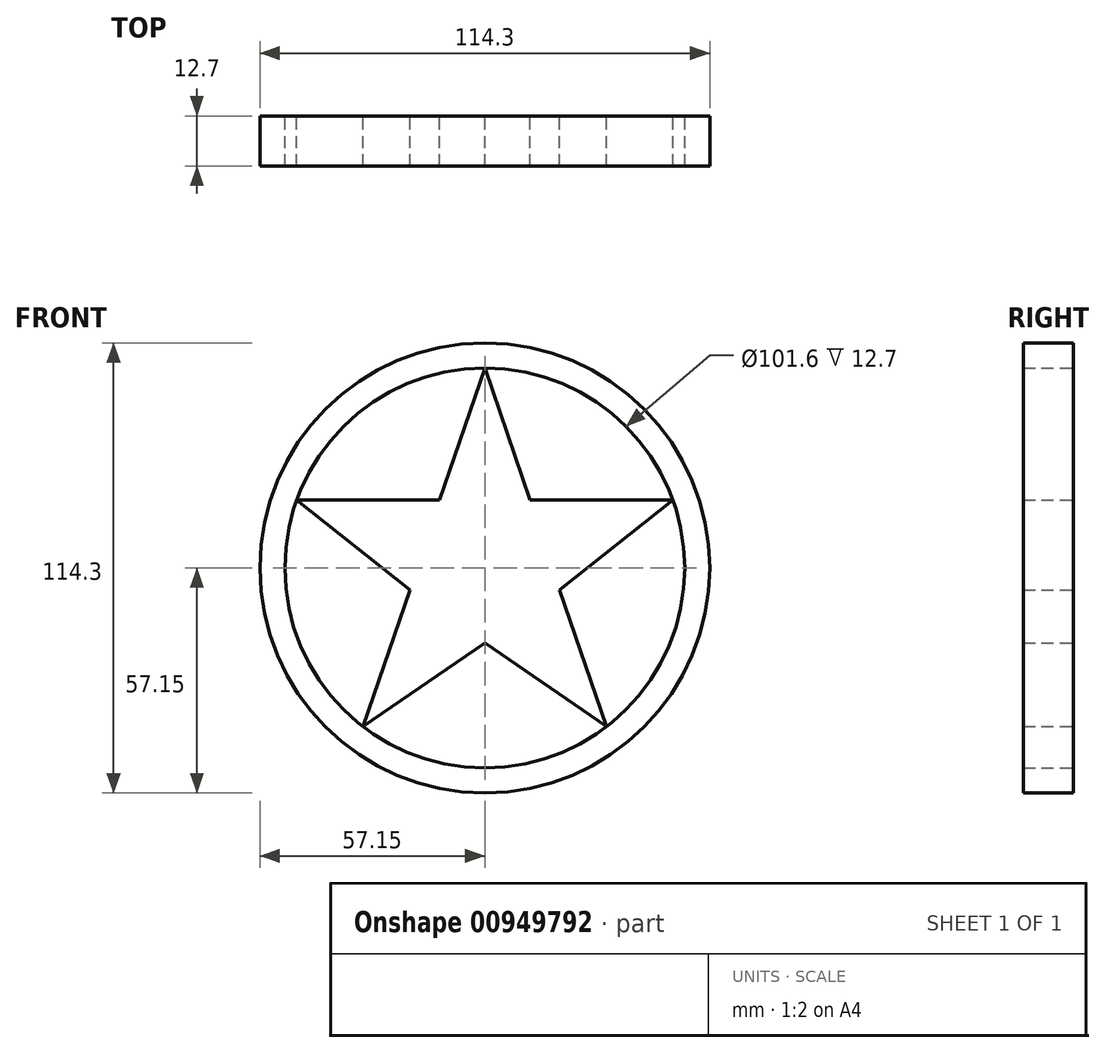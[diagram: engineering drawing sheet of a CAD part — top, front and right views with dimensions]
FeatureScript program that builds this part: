
annotation { "Feature Type Name" : "Feature", "Feature Type Description" : "" }
export const myFeature = defineFeature(function(context is Context, id is Id, definition is map)
    precondition{}
    {
        {
            var Q0;
            Q0=qCreatedBy(makeId("Front.planeOp"),FACE);
            var sketch = newSketch(context, id + "F0", { "sketchPlane" : qUnion([Q0])});
            skCircle(sketch, "E0", {"center": v(0, 0) * mm, "radius": 50.8 * mm});
            skLineSegment(sketch, "E1", {"start": v(0, 50.8) * mm, "end": v(-11.5, 17.3) * mm});
            skLineSegment(sketch, "E2", {"start": v(-11.5, 17.3) * mm, "end": v(-47.76, 17.3) * mm});
            skLineSegment(sketch, "E3", {"start": v(-47.76, 17.3) * mm, "end": v(-19, -5.57) * mm});
            skLineSegment(sketch, "E4", {"start": v(-19, -5.57) * mm, "end": v(-30.93, -40.3) * mm});
            skLineSegment(sketch, "E5", {"start": v(-30.93, -40.3) * mm, "end": v(0, -19.07) * mm});
            skLineSegment(sketch, "E6", {"start": v(0, 91.53) * mm, "end": v(0, -94.74) * mm, "construction": true});
            skLineSegment(sketch, "E7.MirrorCS", {"start": v(30.93, -40.3) * mm, "end": v(0, -19.07) * mm});
            skLineSegment(sketch, "E8.MirrorCS", {"start": v(19, -5.57) * mm, "end": v(30.93, -40.3) * mm});
            skLineSegment(sketch, "E9.MirrorCS", {"start": v(47.76, 17.3) * mm, "end": v(19, -5.57) * mm});
            skLineSegment(sketch, "E10.MirrorCS", {"start": v(0, 50.8) * mm, "end": v(11.5, 17.3) * mm});
            skLineSegment(sketch, "E11.MirrorCS", {"start": v(11.5, 17.3) * mm, "end": v(47.76, 17.3) * mm});
            skCircle(sketch, "E12", {"center": v(0, 0) * mm, "radius": 57.15 * mm});
            skSolve(sketch);
        }
        {
            var Q0;
            Q0=makeQuery(id+"F0.imprint","IMPRINT",FACE,{"disambiguationData":[TD([[makeQuery(id+"F0.imprint","IMPRINT",EDGE,{"derivedFrom":sQuery(id+"F0.wireOp",EDGE,"E12")}),1.0]])]});
            var Q1;
            Q1=makeQuery(id+"F0.imprint","IMPRINT",FACE,{"disambiguationData":[TD([[makeQuery(id+"F0.imprint","IMPRINT",EDGE,{"derivedFrom":sQuery(id+"F0.wireOp",EDGE,"E1")}),1.0]])]});
            extrude(context, id + "F1", {"entities" : qUnion([Q0, Q1]), "depth" : 12.7 * mm, "offsetDistance" : 25.4 * mm});
        }
    });
